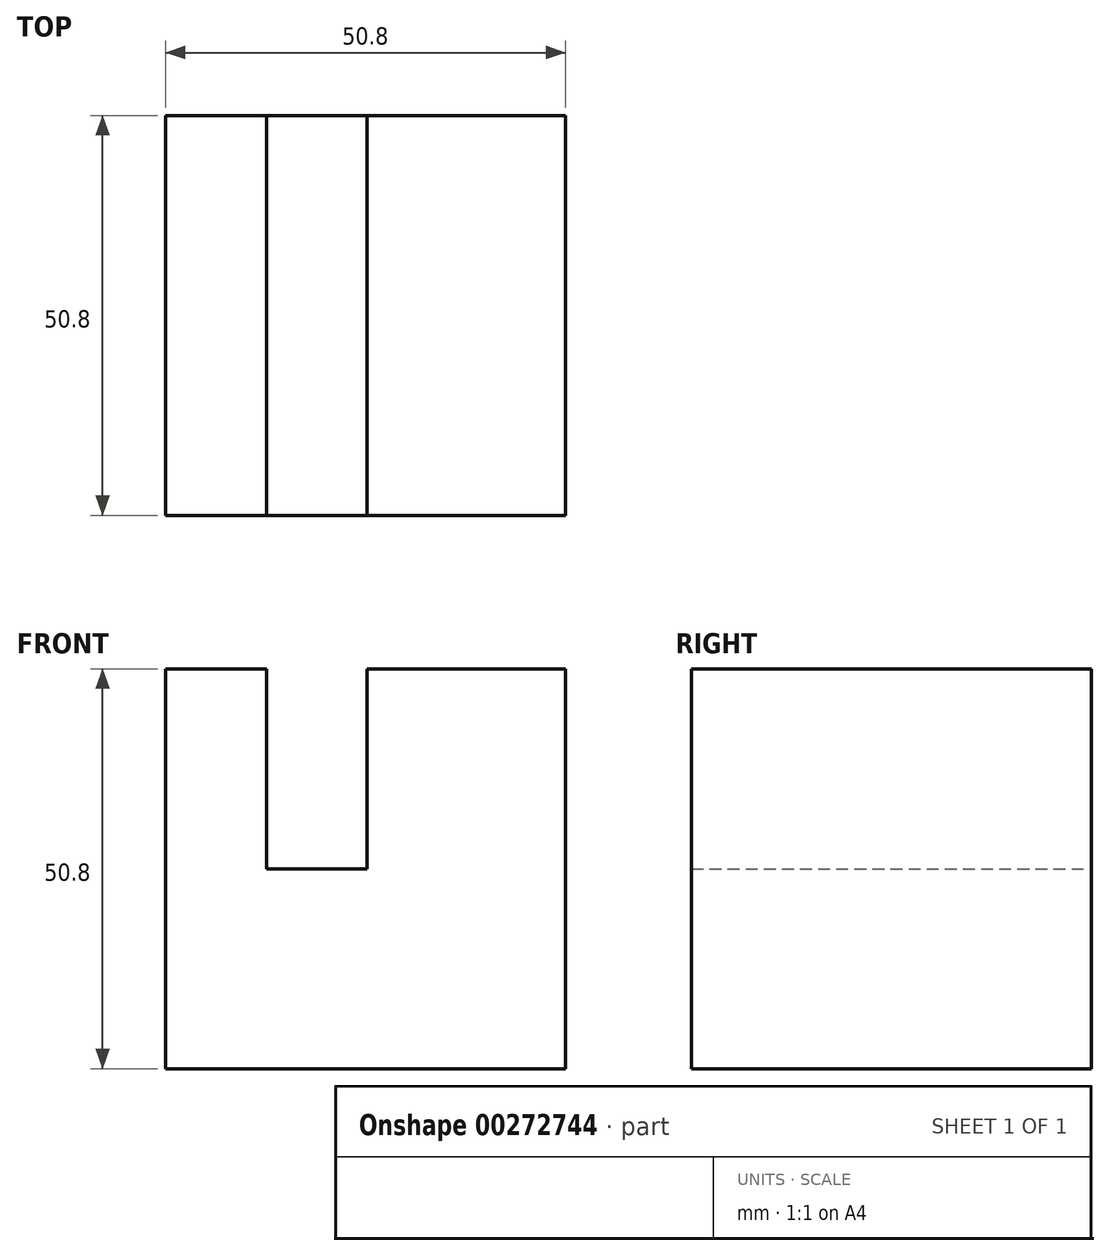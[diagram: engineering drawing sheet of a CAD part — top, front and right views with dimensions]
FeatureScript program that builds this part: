
annotation { "Feature Type Name" : "Feature", "Feature Type Description" : "" }
export const myFeature = defineFeature(function(context is Context, id is Id, definition is map)
    precondition{}
    {
        {
            var Q0;
            Q0=qCreatedBy(makeId("Front.planeOp"),FACE);
            var sketch = newSketch(context, id + "F0", { "sketchPlane" : qUnion([Q0])});
            skLineSegment(sketch, "E0", {"start": v(0, 0) * mm, "end": v(-50.8, 0) * mm});
            skLineSegment(sketch, "E1", {"start": v(-50.8, 0) * mm, "end": v(-50.8, 50.8) * mm});
            skLineSegment(sketch, "E2", {"start": v(-50.8, 50.8) * mm, "end": v(-38, 50.8) * mm});
            skLineSegment(sketch, "E3", {"start": v(-38, 50.8) * mm, "end": v(-38, 25.4) * mm});
            skLineSegment(sketch, "E4", {"start": v(-38, 25.4) * mm, "end": v(-25.2, 25.4) * mm});
            skLineSegment(sketch, "E5", {"start": v(-25.2, 25.4) * mm, "end": v(-25.2, 50.8) * mm});
            skLineSegment(sketch, "E6", {"start": v(-25.2, 50.8) * mm, "end": v(0, 50.8) * mm});
            skLineSegment(sketch, "E7", {"start": v(0, 0) * mm, "end": v(0, 50.8) * mm});
            skSolve(sketch);
        }
        {
            var Q0;
            Q0=makeQuery(id+"F0.imprint","IMPRINT",FACE,{"disambiguationData":[TD([[makeQuery(id+"F0.imprint","IMPRINT",EDGE,{"derivedFrom":sQuery(id+"F0.wireOp",EDGE,"E0")}),-1.0]])]});
            extrude(context, id + "F1", {"entities" : qUnion([Q0]), "depth" : 50.8 * mm});
        }
    });
